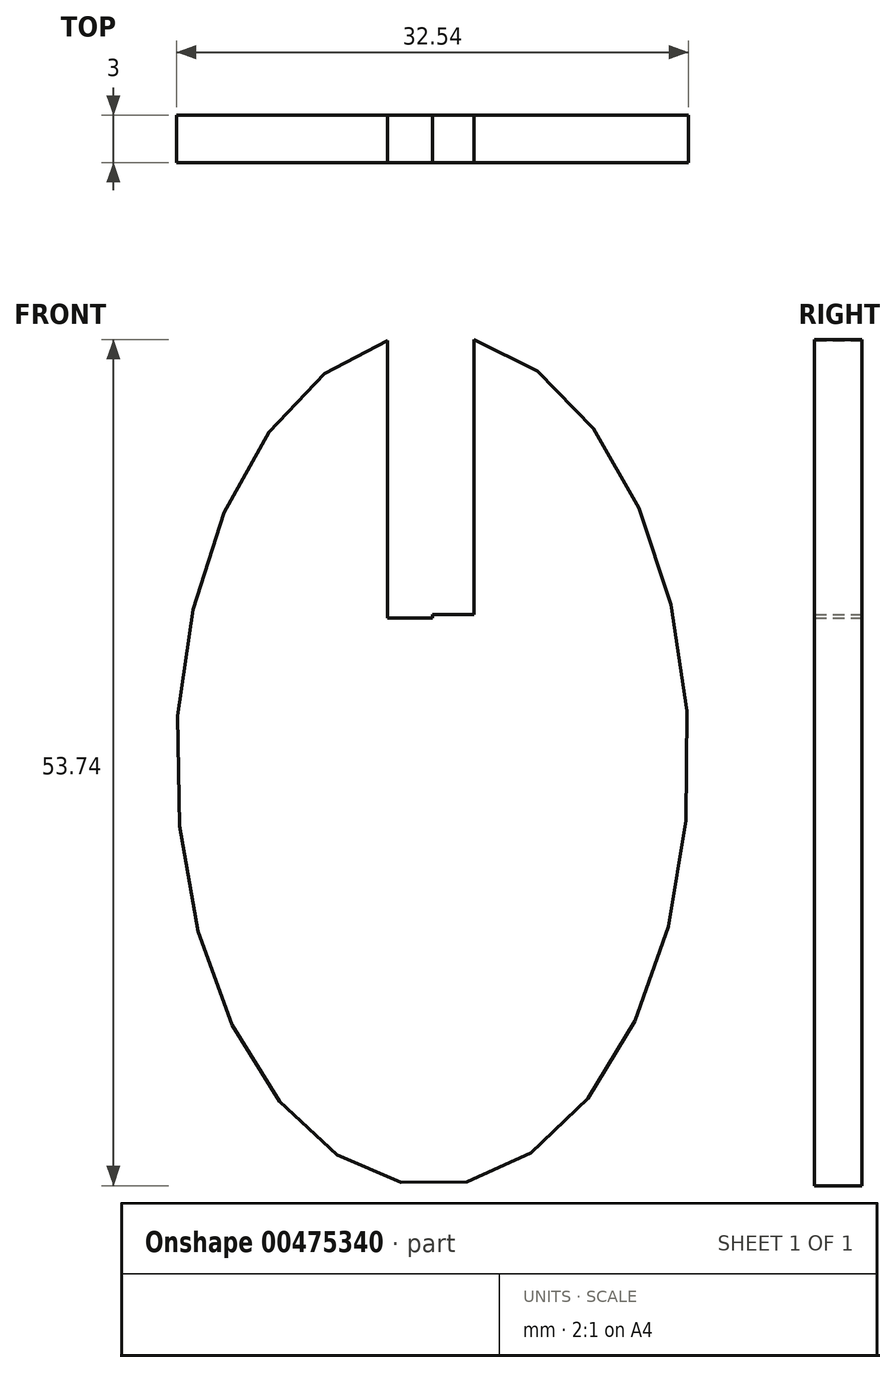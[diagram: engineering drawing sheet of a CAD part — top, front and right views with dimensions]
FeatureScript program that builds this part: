
annotation { "Feature Type Name" : "Feature", "Feature Type Description" : "" }
export const myFeature = defineFeature(function(context is Context, id is Id, definition is map)
    precondition{}
    {
        {
            var Q0;
            Q0=qCreatedBy(makeId("Front.planeOp"),FACE);
            var sketch = newSketch(context, id + "F0", { "sketchPlane" : qUnion([Q0])});
            skEllipticalArc(sketch, "E0", {});
            skLineSegment(sketch, "E1.bottom", {"start": v(0, 27.05) * mm, "end": v(0, 27.05) * mm});
            skLineSegment(sketch, "E1.top", {"start": v(0, 9.23) * mm, "end": v(0, 9.23) * mm});
            skLineSegment(sketch, "E1.left", {"start": v(0, 27.05) * mm, "end": v(0, 26.7) * mm});
            skLineSegment(sketch, "E1.right", {"start": v(0, 27.05) * mm, "end": v(0, 26.7) * mm});
            skLineSegment(sketch, "E2.bottom", {"start": v(0, 9.23) * mm, "end": v(2.65, 9.23) * mm});
            skLineSegment(sketch, "E2.right", {"start": v(2.65, 9.23) * mm, "end": v(2.65, 26.7) * mm});
            skLineSegment(sketch, "E3.top", {"start": v(0, 9) * mm, "end": v(-2.85, 9) * mm});
            skLineSegment(sketch, "E3.right", {"start": v(-2.85, 27.05) * mm, "end": v(-2.85, 9) * mm});
            skLineSegment(sketch, "E4.trimOffspring", {"start": v(0, 9.23) * mm, "end": v(0, 9) * mm});
            const initialGuessF0  = {"E0": [0, 0, 0, 1, 0.027051661163568497, 0.01626833007814186, 0.1759633974456875, 6.1197788004118445]};
            skSetInitialGuess(sketch, initialGuessF0);
            skSolve(sketch);
        }
        {
            var Q0;
            Q0 = qSketchRegion(id + "F0", true);
            extrude(context, id + "F1", {"entities" : qUnion([Q0]), "depth" : 3 * mm});
        }
    });
